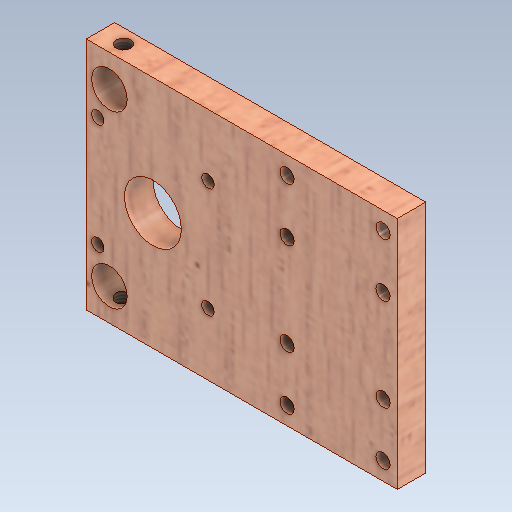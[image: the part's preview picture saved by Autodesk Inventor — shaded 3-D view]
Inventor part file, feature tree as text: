
AUTODESK INVENTOR PART (.ipt)
format: ipt  version: 2020 (Build 240168000, 168)  size: 350,720 bytes
history: native  units: mm
features: sketch x6, other x6, extrude x4, reference x4, hole x3, pattern_linear x2
ambient origin geometry x8: Origin, YZ Plane, XZ Plane, XY Plane, X Axis, Y Axis, Z Axis, Center Point
bodies: Solid1 (feature_tree)
feature tree (25):
  extrude  "Extrusion1"  Depth=66.0mm
  extrude  "Extrusion4"  TaperAngle=0.0deg  [1 undecoded]
  extrude  "Extrusion5"  TaperAngle=0.0deg  [1 undecoded]
  extrude  "Extrusion6"  Depth=9.0mm
  hole  "Hole1"  [1 undecoded]
  pattern_linear  "Rectangular Pattern1"  Spacing1=18.748842mm  [1 undecoded]
  pattern_linear  "Rectangular Pattern2"  Spacing1=3.5mm  [1 undecoded]
  hole  "Hole2"  [1 undecoded]
  hole  "Hole3"  [1 undecoded]
  sketch  "Sketch1"  dims[d0=87.5mm d1=66.0mm]
  sketch  "Sketch4"  dims[d2=8.0mm d3=0.0mm d19=0.0mm d20=0.0mm]
  sketch  "Sketch6"  dims[d24=16.0mm d25=0.0mm d26=0.0mm]
  reference  "Reference7"
  reference  "Reference8"
  sketch  "Sketch8"  dims[d27=6.5mm d28=9.0mm]
  reference  "Reference9"
  reference  "Reference10"
  sketch  "Sketch9"  dims[d29=10.0mm d30=9.0mm]
  sketch  "Sketch10"  dims[d31=0.0mm d32=0.0mm d33=18.748842mm d35=3.5mm d36=31.0mm d38=5.0mm d39=15.0mm d40=26.0mm d41=15.0mm d42=4.0mm d43=4.0mm d44=6.0mm d45=4.0mm d46=2.0mm d47=90.0deg d48=8.0mm d49=20.594885mm d50=20.0mm d52=15.0mm d53=20.0mm d55=41.0mm d56=20.0mm d58=27.0mm d59=6.5mm d60=4.134mm d61=5.0mm d62=4.0mm d63=2.0mm d64=90.0deg d65=7.45mm d66=20.594885mm d67=4.134mm d68=5.0mm d69=4.0mm d70=2.0mm d71=90.0deg d72=7.45mm d73=20.594885mm]
  parser-record x1  (decoder bookkeeping rows leaked as tree rows — omitted from the tree; the rows remain in map.json)
  other  "0005-00-00 Ansamblu_General.iam"
  other  "0005-10-1001 NEMA17 - Motor de passo.ipt:23"
  other  "0005-10-04 Z axis and extruder.iam"
  other  "0005-10-10-1003 LeadScrew 8mm x 2mmPitch.ipt:21"
  other  "0005-10-1002  Hub.ipt:22"
note: 7 required parameter values undecoded (feature->parameter linkage not recoverable at this tier; creation-order binding heuristic only, values carry confidence <= 0.55)
note: 1 file-system path scrubbed to <path> (originals preserved in map.json)
